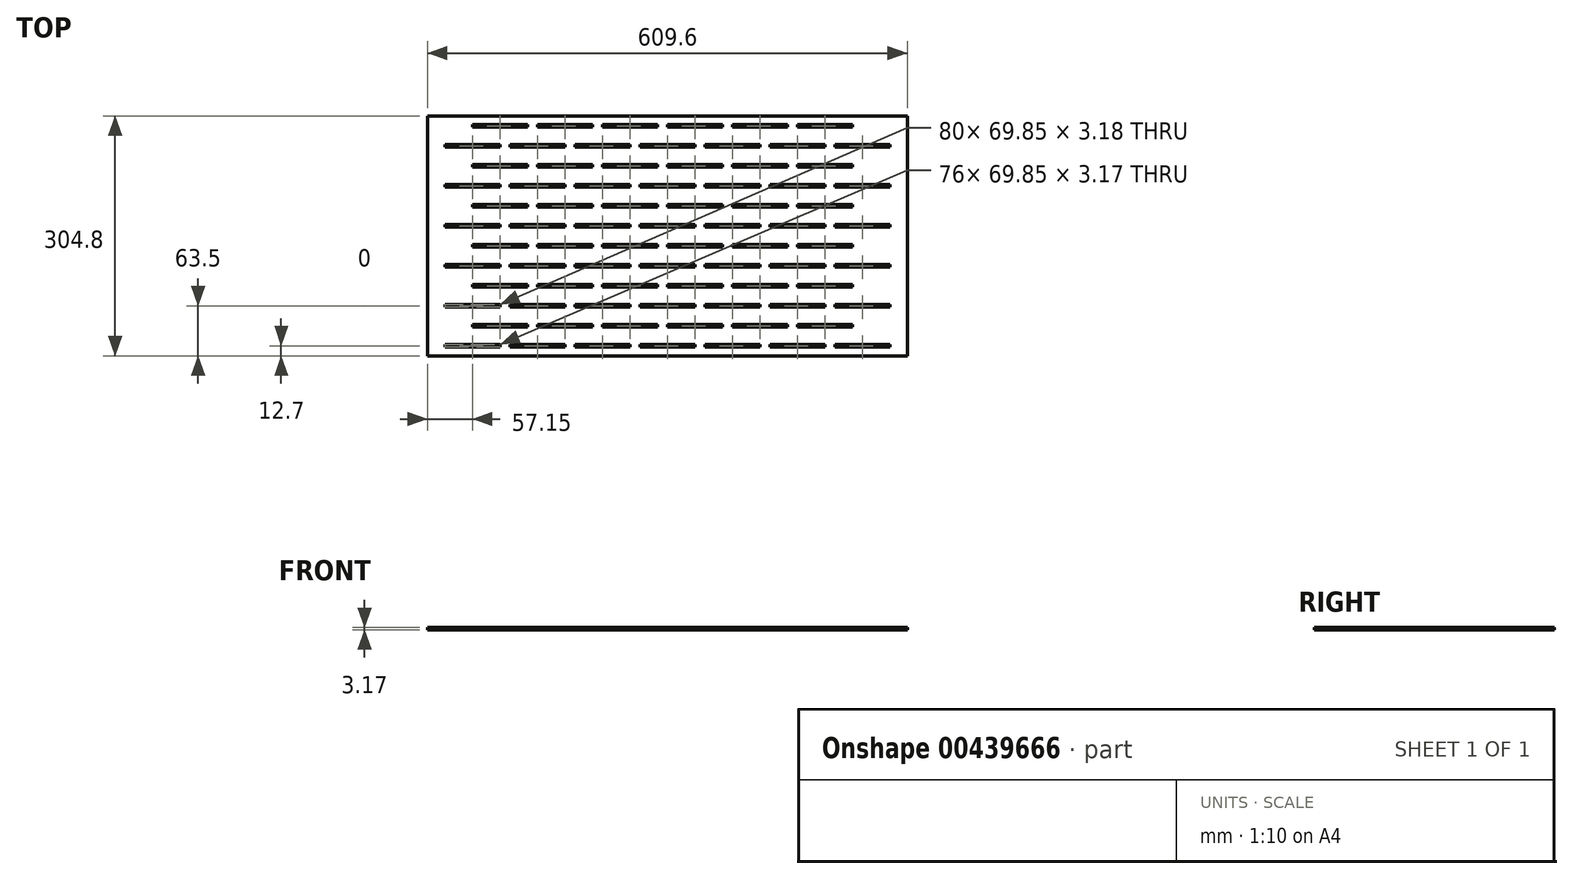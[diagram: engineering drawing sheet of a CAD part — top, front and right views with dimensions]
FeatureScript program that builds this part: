
annotation { "Feature Type Name" : "Feature", "Feature Type Description" : "" }
export const myFeature = defineFeature(function(context is Context, id is Id, definition is map)
    precondition{}
    {
        {
            var Q0;
            Q0=qCreatedBy(makeId("Top.planeOp"),FACE);
            var sketch = newSketch(context, id + "F0", { "sketchPlane" : qUnion([Q0])});
            skLineSegment(sketch, "E0.bottom", {"start": v(0, 0) * mm, "end": v(609.6, 0) * mm});
            skLineSegment(sketch, "E0.top", {"start": v(0, 304.8) * mm, "end": v(609.6, 304.8) * mm});
            skLineSegment(sketch, "E0.left", {"start": v(0, 0) * mm, "end": v(0, 304.8) * mm});
            skLineSegment(sketch, "E0.right", {"start": v(609.6, 0) * mm, "end": v(609.6, 304.8) * mm});
            skLineSegment(sketch, "E1.bottom", {"start": v(22.22, 14.29) * mm, "end": v(92.07, 14.29) * mm});
            skLineSegment(sketch, "E1.top", {"start": v(22.23, 11.11) * mm, "end": v(92.07, 11.11) * mm});
            skLineSegment(sketch, "E1.left", {"start": v(22.22, 14.29) * mm, "end": v(22.22, 11.11) * mm});
            skLineSegment(sketch, "E1.right", {"start": v(92.08, 14.29) * mm, "end": v(92.08, 11.11) * mm});
            skLineSegment(sketch, "E2.1.0.0", {"start": v(104.78, 11.11) * mm, "end": v(174.62, 11.11) * mm});
            skLineSegment(sketch, "E2.1.0.1", {"start": v(104.77, 14.29) * mm, "end": v(174.62, 14.29) * mm});
            skLineSegment(sketch, "E2.1.0.2", {"start": v(104.78, 14.29) * mm, "end": v(104.78, 11.11) * mm});
            skLineSegment(sketch, "E2.1.0.3", {"start": v(174.63, 14.29) * mm, "end": v(174.63, 11.11) * mm});
            skLineSegment(sketch, "E2.2.0.0", {"start": v(187.33, 11.11) * mm, "end": v(257.18, 11.11) * mm});
            skLineSegment(sketch, "E2.2.0.1", {"start": v(187.32, 14.29) * mm, "end": v(257.18, 14.29) * mm});
            skLineSegment(sketch, "E2.2.0.2", {"start": v(187.33, 14.29) * mm, "end": v(187.33, 11.11) * mm});
            skLineSegment(sketch, "E2.2.0.3", {"start": v(257.18, 14.29) * mm, "end": v(257.18, 11.11) * mm});
            skLineSegment(sketch, "E2.3.0.0", {"start": v(269.88, 11.11) * mm, "end": v(339.73, 11.11) * mm});
            skLineSegment(sketch, "E2.3.0.1", {"start": v(269.88, 14.29) * mm, "end": v(339.73, 14.29) * mm});
            skLineSegment(sketch, "E2.3.0.2", {"start": v(269.88, 14.29) * mm, "end": v(269.88, 11.11) * mm});
            skLineSegment(sketch, "E2.3.0.3", {"start": v(339.73, 14.29) * mm, "end": v(339.73, 11.11) * mm});
            skLineSegment(sketch, "E2.4.0.0", {"start": v(352.43, 11.11) * mm, "end": v(422.28, 11.11) * mm});
            skLineSegment(sketch, "E2.4.0.1", {"start": v(352.43, 14.29) * mm, "end": v(422.28, 14.29) * mm});
            skLineSegment(sketch, "E2.4.0.2", {"start": v(352.43, 14.29) * mm, "end": v(352.43, 11.11) * mm});
            skLineSegment(sketch, "E2.4.0.3", {"start": v(422.28, 14.29) * mm, "end": v(422.28, 11.11) * mm});
            skLineSegment(sketch, "E2.5.0.0", {"start": v(434.98, 11.11) * mm, "end": v(504.83, 11.11) * mm});
            skLineSegment(sketch, "E2.5.0.1", {"start": v(434.98, 14.29) * mm, "end": v(504.83, 14.29) * mm});
            skLineSegment(sketch, "E2.5.0.2", {"start": v(434.98, 14.29) * mm, "end": v(434.98, 11.11) * mm});
            skLineSegment(sketch, "E2.5.0.3", {"start": v(504.83, 14.29) * mm, "end": v(504.83, 11.11) * mm});
            skLineSegment(sketch, "E2.6.0.0", {"start": v(517.53, 11.11) * mm, "end": v(587.38, 11.11) * mm});
            skLineSegment(sketch, "E2.6.0.1", {"start": v(517.52, 14.29) * mm, "end": v(587.38, 14.29) * mm});
            skLineSegment(sketch, "E2.6.0.2", {"start": v(517.52, 14.29) * mm, "end": v(517.52, 11.11) * mm});
            skLineSegment(sketch, "E2.6.0.3", {"start": v(587.38, 14.29) * mm, "end": v(587.38, 11.11) * mm});
            skLineSegment(sketch, "E2.direction1", {"start": v(22.23, 11.11) * mm, "end": v(104.78, 11.11) * mm, "construction": true});
            skLineSegment(sketch, "E3.direction1", {"start": v(22.23, 11.11) * mm, "end": v(47.62, 11.11) * mm, "construction": true});
            skLineSegment(sketch, "E4.0.1.0", {"start": v(187.33, 61.91) * mm, "end": v(257.18, 61.91) * mm});
            skLineSegment(sketch, "E4.0.1.1", {"start": v(352.43, 61.91) * mm, "end": v(422.28, 61.91) * mm});
            skLineSegment(sketch, "E4.0.1.2", {"start": v(517.52, 65.09) * mm, "end": v(587.38, 65.09) * mm});
            skLineSegment(sketch, "E4.0.1.3", {"start": v(269.88, 61.91) * mm, "end": v(339.73, 61.91) * mm});
            skLineSegment(sketch, "E4.0.1.4", {"start": v(22.23, 61.91) * mm, "end": v(104.78, 61.91) * mm, "construction": true});
            skLineSegment(sketch, "E4.0.1.5", {"start": v(517.53, 61.91) * mm, "end": v(587.38, 61.91) * mm});
            skLineSegment(sketch, "E4.0.1.6", {"start": v(434.98, 61.91) * mm, "end": v(504.83, 61.91) * mm});
            skLineSegment(sketch, "E4.0.1.7", {"start": v(352.43, 65.09) * mm, "end": v(422.28, 65.09) * mm});
            skLineSegment(sketch, "E4.0.1.8", {"start": v(434.98, 65.09) * mm, "end": v(504.83, 65.09) * mm});
            skLineSegment(sketch, "E4.0.1.9", {"start": v(22.22, 65.09) * mm, "end": v(92.07, 65.09) * mm});
            skLineSegment(sketch, "E4.0.1.10", {"start": v(187.32, 65.09) * mm, "end": v(257.18, 65.09) * mm});
            skLineSegment(sketch, "E4.0.1.11", {"start": v(104.78, 61.91) * mm, "end": v(174.62, 61.91) * mm});
            skLineSegment(sketch, "E4.0.1.12", {"start": v(104.77, 65.09) * mm, "end": v(174.62, 65.09) * mm});
            skLineSegment(sketch, "E4.0.1.13", {"start": v(269.88, 65.09) * mm, "end": v(339.73, 65.09) * mm});
            skLineSegment(sketch, "E4.0.1.14", {"start": v(22.23, 61.91) * mm, "end": v(92.07, 61.91) * mm});
            skLineSegment(sketch, "E4.0.1.15", {"start": v(22.23, 61.91) * mm, "end": v(47.62, 61.91) * mm, "construction": true});
            skLineSegment(sketch, "E4.0.1.16", {"start": v(422.28, 65.09) * mm, "end": v(422.28, 61.91) * mm});
            skLineSegment(sketch, "E4.0.1.17", {"start": v(517.52, 65.09) * mm, "end": v(517.52, 61.91) * mm});
            skLineSegment(sketch, "E4.0.1.18", {"start": v(352.43, 65.09) * mm, "end": v(352.43, 61.91) * mm});
            skLineSegment(sketch, "E4.0.1.19", {"start": v(587.38, 65.09) * mm, "end": v(587.38, 61.91) * mm});
            skLineSegment(sketch, "E4.0.1.20", {"start": v(92.08, 65.09) * mm, "end": v(92.08, 61.91) * mm});
            skLineSegment(sketch, "E4.0.1.21", {"start": v(187.33, 65.09) * mm, "end": v(187.33, 61.91) * mm});
            skLineSegment(sketch, "E4.0.1.22", {"start": v(257.18, 65.09) * mm, "end": v(257.18, 61.91) * mm});
            skLineSegment(sketch, "E4.0.1.23", {"start": v(504.83, 65.09) * mm, "end": v(504.83, 61.91) * mm});
            skLineSegment(sketch, "E4.0.1.24", {"start": v(174.63, 65.09) * mm, "end": v(174.63, 61.91) * mm});
            skLineSegment(sketch, "E4.0.1.25", {"start": v(434.98, 65.09) * mm, "end": v(434.98, 61.91) * mm});
            skLineSegment(sketch, "E4.0.1.26", {"start": v(269.88, 65.09) * mm, "end": v(269.88, 61.91) * mm});
            skLineSegment(sketch, "E4.0.1.27", {"start": v(339.73, 65.09) * mm, "end": v(339.73, 61.91) * mm});
            skLineSegment(sketch, "E4.0.1.28", {"start": v(22.22, 65.09) * mm, "end": v(22.22, 61.91) * mm});
            skLineSegment(sketch, "E4.0.1.29", {"start": v(104.78, 65.09) * mm, "end": v(104.78, 61.91) * mm});
            skLineSegment(sketch, "E4.0.2.0", {"start": v(187.33, 112.71) * mm, "end": v(257.18, 112.71) * mm});
            skLineSegment(sketch, "E4.0.2.1", {"start": v(352.43, 112.71) * mm, "end": v(422.28, 112.71) * mm});
            skLineSegment(sketch, "E4.0.2.2", {"start": v(517.52, 115.89) * mm, "end": v(587.38, 115.89) * mm});
            skLineSegment(sketch, "E4.0.2.3", {"start": v(269.88, 112.71) * mm, "end": v(339.73, 112.71) * mm});
            skLineSegment(sketch, "E4.0.2.4", {"start": v(22.23, 112.71) * mm, "end": v(104.78, 112.71) * mm, "construction": true});
            skLineSegment(sketch, "E4.0.2.5", {"start": v(517.53, 112.71) * mm, "end": v(587.38, 112.71) * mm});
            skLineSegment(sketch, "E4.0.2.6", {"start": v(434.98, 112.71) * mm, "end": v(504.83, 112.71) * mm});
            skLineSegment(sketch, "E4.0.2.7", {"start": v(352.43, 115.89) * mm, "end": v(422.28, 115.89) * mm});
            skLineSegment(sketch, "E4.0.2.8", {"start": v(434.98, 115.89) * mm, "end": v(504.83, 115.89) * mm});
            skLineSegment(sketch, "E4.0.2.9", {"start": v(22.22, 115.89) * mm, "end": v(92.07, 115.89) * mm});
            skLineSegment(sketch, "E4.0.2.10", {"start": v(187.32, 115.89) * mm, "end": v(257.18, 115.89) * mm});
            skLineSegment(sketch, "E4.0.2.11", {"start": v(104.78, 112.71) * mm, "end": v(174.62, 112.71) * mm});
            skLineSegment(sketch, "E4.0.2.12", {"start": v(104.77, 115.89) * mm, "end": v(174.62, 115.89) * mm});
            skLineSegment(sketch, "E4.0.2.13", {"start": v(269.88, 115.89) * mm, "end": v(339.73, 115.89) * mm});
            skLineSegment(sketch, "E4.0.2.14", {"start": v(22.23, 112.71) * mm, "end": v(92.07, 112.71) * mm});
            skLineSegment(sketch, "E4.0.2.15", {"start": v(22.23, 112.71) * mm, "end": v(47.62, 112.71) * mm, "construction": true});
            skLineSegment(sketch, "E4.0.2.16", {"start": v(422.28, 115.89) * mm, "end": v(422.28, 112.71) * mm});
            skLineSegment(sketch, "E4.0.2.17", {"start": v(517.52, 115.89) * mm, "end": v(517.52, 112.71) * mm});
            skLineSegment(sketch, "E4.0.2.18", {"start": v(352.43, 115.89) * mm, "end": v(352.43, 112.71) * mm});
            skLineSegment(sketch, "E4.0.2.19", {"start": v(587.38, 115.89) * mm, "end": v(587.38, 112.71) * mm});
            skLineSegment(sketch, "E4.0.2.20", {"start": v(92.08, 115.89) * mm, "end": v(92.08, 112.71) * mm});
            skLineSegment(sketch, "E4.0.2.21", {"start": v(187.33, 115.89) * mm, "end": v(187.33, 112.71) * mm});
            skLineSegment(sketch, "E4.0.2.22", {"start": v(257.18, 115.89) * mm, "end": v(257.18, 112.71) * mm});
            skLineSegment(sketch, "E4.0.2.23", {"start": v(504.83, 115.89) * mm, "end": v(504.83, 112.71) * mm});
            skLineSegment(sketch, "E4.0.2.24", {"start": v(174.63, 115.89) * mm, "end": v(174.63, 112.71) * mm});
            skLineSegment(sketch, "E4.0.2.25", {"start": v(434.98, 115.89) * mm, "end": v(434.98, 112.71) * mm});
            skLineSegment(sketch, "E4.0.2.26", {"start": v(269.88, 115.89) * mm, "end": v(269.88, 112.71) * mm});
            skLineSegment(sketch, "E4.0.2.27", {"start": v(339.73, 115.89) * mm, "end": v(339.73, 112.71) * mm});
            skLineSegment(sketch, "E4.0.2.28", {"start": v(22.22, 115.89) * mm, "end": v(22.22, 112.71) * mm});
            skLineSegment(sketch, "E4.0.2.29", {"start": v(104.78, 115.89) * mm, "end": v(104.78, 112.71) * mm});
            skLineSegment(sketch, "E4.0.3.0", {"start": v(187.33, 163.51) * mm, "end": v(257.18, 163.51) * mm});
            skLineSegment(sketch, "E4.0.3.1", {"start": v(352.43, 163.51) * mm, "end": v(422.28, 163.51) * mm});
            skLineSegment(sketch, "E4.0.3.2", {"start": v(517.52, 166.69) * mm, "end": v(587.38, 166.69) * mm});
            skLineSegment(sketch, "E4.0.3.3", {"start": v(269.88, 163.51) * mm, "end": v(339.73, 163.51) * mm});
            skLineSegment(sketch, "E4.0.3.4", {"start": v(22.23, 163.51) * mm, "end": v(104.78, 163.51) * mm, "construction": true});
            skLineSegment(sketch, "E4.0.3.5", {"start": v(517.53, 163.51) * mm, "end": v(587.38, 163.51) * mm});
            skLineSegment(sketch, "E4.0.3.6", {"start": v(434.98, 163.51) * mm, "end": v(504.83, 163.51) * mm});
            skLineSegment(sketch, "E4.0.3.7", {"start": v(352.43, 166.69) * mm, "end": v(422.28, 166.69) * mm});
            skLineSegment(sketch, "E4.0.3.8", {"start": v(434.98, 166.69) * mm, "end": v(504.83, 166.69) * mm});
            skLineSegment(sketch, "E4.0.3.9", {"start": v(22.22, 166.69) * mm, "end": v(92.07, 166.69) * mm});
            skLineSegment(sketch, "E4.0.3.10", {"start": v(187.32, 166.69) * mm, "end": v(257.18, 166.69) * mm});
            skLineSegment(sketch, "E4.0.3.11", {"start": v(104.78, 163.51) * mm, "end": v(174.62, 163.51) * mm});
            skLineSegment(sketch, "E4.0.3.12", {"start": v(104.77, 166.69) * mm, "end": v(174.62, 166.69) * mm});
            skLineSegment(sketch, "E4.0.3.13", {"start": v(269.88, 166.69) * mm, "end": v(339.73, 166.69) * mm});
            skLineSegment(sketch, "E4.0.3.14", {"start": v(22.23, 163.51) * mm, "end": v(92.07, 163.51) * mm});
            skLineSegment(sketch, "E4.0.3.15", {"start": v(22.23, 163.51) * mm, "end": v(47.62, 163.51) * mm, "construction": true});
            skLineSegment(sketch, "E4.0.3.16", {"start": v(422.28, 166.69) * mm, "end": v(422.28, 163.51) * mm});
            skLineSegment(sketch, "E4.0.3.17", {"start": v(517.52, 166.69) * mm, "end": v(517.52, 163.51) * mm});
            skLineSegment(sketch, "E4.0.3.18", {"start": v(352.43, 166.69) * mm, "end": v(352.43, 163.51) * mm});
            skLineSegment(sketch, "E4.0.3.19", {"start": v(587.38, 166.69) * mm, "end": v(587.38, 163.51) * mm});
            skLineSegment(sketch, "E4.0.3.20", {"start": v(92.08, 166.69) * mm, "end": v(92.08, 163.51) * mm});
            skLineSegment(sketch, "E4.0.3.21", {"start": v(187.33, 166.69) * mm, "end": v(187.33, 163.51) * mm});
            skLineSegment(sketch, "E4.0.3.22", {"start": v(257.18, 166.69) * mm, "end": v(257.18, 163.51) * mm});
            skLineSegment(sketch, "E4.0.3.23", {"start": v(504.83, 166.69) * mm, "end": v(504.83, 163.51) * mm});
            skLineSegment(sketch, "E4.0.3.24", {"start": v(174.63, 166.69) * mm, "end": v(174.63, 163.51) * mm});
            skLineSegment(sketch, "E4.0.3.25", {"start": v(434.98, 166.69) * mm, "end": v(434.98, 163.51) * mm});
            skLineSegment(sketch, "E4.0.3.26", {"start": v(269.88, 166.69) * mm, "end": v(269.88, 163.51) * mm});
            skLineSegment(sketch, "E4.0.3.27", {"start": v(339.73, 166.69) * mm, "end": v(339.73, 163.51) * mm});
            skLineSegment(sketch, "E4.0.3.28", {"start": v(22.22, 166.69) * mm, "end": v(22.22, 163.51) * mm});
            skLineSegment(sketch, "E4.0.3.29", {"start": v(104.78, 166.69) * mm, "end": v(104.78, 163.51) * mm});
            skLineSegment(sketch, "E4.0.4.0", {"start": v(187.33, 214.31) * mm, "end": v(257.18, 214.31) * mm});
            skLineSegment(sketch, "E4.0.4.1", {"start": v(352.43, 214.31) * mm, "end": v(422.28, 214.31) * mm});
            skLineSegment(sketch, "E4.0.4.2", {"start": v(517.52, 217.49) * mm, "end": v(587.38, 217.49) * mm});
            skLineSegment(sketch, "E4.0.4.3", {"start": v(269.88, 214.31) * mm, "end": v(339.73, 214.31) * mm});
            skLineSegment(sketch, "E4.0.4.4", {"start": v(22.23, 214.31) * mm, "end": v(104.78, 214.31) * mm, "construction": true});
            skLineSegment(sketch, "E4.0.4.5", {"start": v(517.53, 214.31) * mm, "end": v(587.38, 214.31) * mm});
            skLineSegment(sketch, "E4.0.4.6", {"start": v(434.98, 214.31) * mm, "end": v(504.83, 214.31) * mm});
            skLineSegment(sketch, "E4.0.4.7", {"start": v(352.43, 217.49) * mm, "end": v(422.28, 217.49) * mm});
            skLineSegment(sketch, "E4.0.4.8", {"start": v(434.98, 217.49) * mm, "end": v(504.83, 217.49) * mm});
            skLineSegment(sketch, "E4.0.4.9", {"start": v(22.22, 217.49) * mm, "end": v(92.07, 217.49) * mm});
            skLineSegment(sketch, "E4.0.4.10", {"start": v(187.32, 217.49) * mm, "end": v(257.18, 217.49) * mm});
            skLineSegment(sketch, "E4.0.4.11", {"start": v(104.78, 214.31) * mm, "end": v(174.62, 214.31) * mm});
            skLineSegment(sketch, "E4.0.4.12", {"start": v(104.77, 217.49) * mm, "end": v(174.62, 217.49) * mm});
            skLineSegment(sketch, "E4.0.4.13", {"start": v(269.88, 217.49) * mm, "end": v(339.73, 217.49) * mm});
            skLineSegment(sketch, "E4.0.4.14", {"start": v(22.23, 214.31) * mm, "end": v(92.07, 214.31) * mm});
            skLineSegment(sketch, "E4.0.4.15", {"start": v(22.23, 214.31) * mm, "end": v(47.62, 214.31) * mm, "construction": true});
            skLineSegment(sketch, "E4.0.4.16", {"start": v(422.28, 217.49) * mm, "end": v(422.28, 214.31) * mm});
            skLineSegment(sketch, "E4.0.4.17", {"start": v(517.52, 217.49) * mm, "end": v(517.52, 214.31) * mm});
            skLineSegment(sketch, "E4.0.4.18", {"start": v(352.43, 217.49) * mm, "end": v(352.43, 214.31) * mm});
            skLineSegment(sketch, "E4.0.4.19", {"start": v(587.38, 217.49) * mm, "end": v(587.38, 214.31) * mm});
            skLineSegment(sketch, "E4.0.4.20", {"start": v(92.08, 217.49) * mm, "end": v(92.08, 214.31) * mm});
            skLineSegment(sketch, "E4.0.4.21", {"start": v(187.33, 217.49) * mm, "end": v(187.33, 214.31) * mm});
            skLineSegment(sketch, "E4.0.4.22", {"start": v(257.18, 217.49) * mm, "end": v(257.18, 214.31) * mm});
            skLineSegment(sketch, "E4.0.4.23", {"start": v(504.83, 217.49) * mm, "end": v(504.83, 214.31) * mm});
            skLineSegment(sketch, "E4.0.4.24", {"start": v(174.63, 217.49) * mm, "end": v(174.63, 214.31) * mm});
            skLineSegment(sketch, "E4.0.4.25", {"start": v(434.98, 217.49) * mm, "end": v(434.98, 214.31) * mm});
            skLineSegment(sketch, "E4.0.4.26", {"start": v(269.88, 217.49) * mm, "end": v(269.88, 214.31) * mm});
            skLineSegment(sketch, "E4.0.4.27", {"start": v(339.73, 217.49) * mm, "end": v(339.73, 214.31) * mm});
            skLineSegment(sketch, "E4.0.4.28", {"start": v(22.22, 217.49) * mm, "end": v(22.22, 214.31) * mm});
            skLineSegment(sketch, "E4.0.4.29", {"start": v(104.78, 217.49) * mm, "end": v(104.78, 214.31) * mm});
            skLineSegment(sketch, "E4.0.5.0", {"start": v(187.33, 265.11) * mm, "end": v(257.18, 265.11) * mm});
            skLineSegment(sketch, "E4.0.5.1", {"start": v(352.43, 265.11) * mm, "end": v(422.28, 265.11) * mm});
            skLineSegment(sketch, "E4.0.5.2", {"start": v(517.52, 268.29) * mm, "end": v(587.38, 268.29) * mm});
            skLineSegment(sketch, "E4.0.5.3", {"start": v(269.88, 265.11) * mm, "end": v(339.73, 265.11) * mm});
            skLineSegment(sketch, "E4.0.5.4", {"start": v(22.23, 265.11) * mm, "end": v(104.78, 265.11) * mm, "construction": true});
            skLineSegment(sketch, "E4.0.5.5", {"start": v(517.53, 265.11) * mm, "end": v(587.38, 265.11) * mm});
            skLineSegment(sketch, "E4.0.5.6", {"start": v(434.98, 265.11) * mm, "end": v(504.83, 265.11) * mm});
            skLineSegment(sketch, "E4.0.5.7", {"start": v(352.43, 268.29) * mm, "end": v(422.28, 268.29) * mm});
            skLineSegment(sketch, "E4.0.5.8", {"start": v(434.98, 268.29) * mm, "end": v(504.83, 268.29) * mm});
            skLineSegment(sketch, "E4.0.5.9", {"start": v(22.22, 268.29) * mm, "end": v(92.07, 268.29) * mm});
            skLineSegment(sketch, "E4.0.5.10", {"start": v(187.32, 268.29) * mm, "end": v(257.18, 268.29) * mm});
            skLineSegment(sketch, "E4.0.5.11", {"start": v(104.78, 265.11) * mm, "end": v(174.62, 265.11) * mm});
            skLineSegment(sketch, "E4.0.5.12", {"start": v(104.77, 268.29) * mm, "end": v(174.62, 268.29) * mm});
            skLineSegment(sketch, "E4.0.5.13", {"start": v(269.88, 268.29) * mm, "end": v(339.73, 268.29) * mm});
            skLineSegment(sketch, "E4.0.5.14", {"start": v(22.23, 265.11) * mm, "end": v(92.07, 265.11) * mm});
            skLineSegment(sketch, "E4.0.5.15", {"start": v(22.23, 265.11) * mm, "end": v(47.62, 265.11) * mm, "construction": true});
            skLineSegment(sketch, "E4.0.5.16", {"start": v(422.28, 268.29) * mm, "end": v(422.28, 265.11) * mm});
            skLineSegment(sketch, "E4.0.5.17", {"start": v(517.52, 268.29) * mm, "end": v(517.52, 265.11) * mm});
            skLineSegment(sketch, "E4.0.5.18", {"start": v(352.43, 268.29) * mm, "end": v(352.43, 265.11) * mm});
            skLineSegment(sketch, "E4.0.5.19", {"start": v(587.38, 268.29) * mm, "end": v(587.38, 265.11) * mm});
            skLineSegment(sketch, "E4.0.5.20", {"start": v(92.08, 268.29) * mm, "end": v(92.08, 265.11) * mm});
            skLineSegment(sketch, "E4.0.5.21", {"start": v(187.33, 268.29) * mm, "end": v(187.33, 265.11) * mm});
            skLineSegment(sketch, "E4.0.5.22", {"start": v(257.18, 268.29) * mm, "end": v(257.18, 265.11) * mm});
            skLineSegment(sketch, "E4.0.5.23", {"start": v(504.83, 268.29) * mm, "end": v(504.83, 265.11) * mm});
            skLineSegment(sketch, "E4.0.5.24", {"start": v(174.63, 268.29) * mm, "end": v(174.63, 265.11) * mm});
            skLineSegment(sketch, "E4.0.5.25", {"start": v(434.98, 268.29) * mm, "end": v(434.98, 265.11) * mm});
            skLineSegment(sketch, "E4.0.5.26", {"start": v(269.88, 268.29) * mm, "end": v(269.88, 265.11) * mm});
            skLineSegment(sketch, "E4.0.5.27", {"start": v(339.73, 268.29) * mm, "end": v(339.73, 265.11) * mm});
            skLineSegment(sketch, "E4.0.5.28", {"start": v(22.22, 268.29) * mm, "end": v(22.22, 265.11) * mm});
            skLineSegment(sketch, "E4.0.5.29", {"start": v(104.78, 268.29) * mm, "end": v(104.78, 265.11) * mm});
            skLineSegment(sketch, "E4.direction1", {"start": v(22.22, 11.11) * mm, "end": v(47.62, 11.11) * mm, "construction": true});
            skLineSegment(sketch, "E4.direction2", {"start": v(22.22, 11.11) * mm, "end": v(22.22, 61.91) * mm, "construction": true});
            skLineSegment(sketch, "E5.bottom", {"start": v(57.15, 39.69) * mm, "end": v(127, 39.69) * mm});
            skLineSegment(sketch, "E5.top", {"start": v(57.15, 36.51) * mm, "end": v(127, 36.51) * mm});
            skLineSegment(sketch, "E5.left", {"start": v(57.15, 39.69) * mm, "end": v(57.15, 36.51) * mm});
            skLineSegment(sketch, "E5.right", {"start": v(127, 39.69) * mm, "end": v(127, 36.51) * mm});
            skLineSegment(sketch, "E6.1.0.0", {"start": v(139.7, 36.51) * mm, "end": v(209.55, 36.51) * mm});
            skLineSegment(sketch, "E6.1.0.1", {"start": v(139.7, 39.69) * mm, "end": v(209.55, 39.69) * mm});
            skLineSegment(sketch, "E6.1.0.2", {"start": v(139.7, 39.69) * mm, "end": v(139.7, 36.51) * mm});
            skLineSegment(sketch, "E6.1.0.3", {"start": v(209.55, 39.69) * mm, "end": v(209.55, 36.51) * mm});
            skLineSegment(sketch, "E6.2.0.0", {"start": v(222.25, 36.51) * mm, "end": v(292.1, 36.51) * mm});
            skLineSegment(sketch, "E6.2.0.1", {"start": v(222.25, 39.69) * mm, "end": v(292.1, 39.69) * mm});
            skLineSegment(sketch, "E6.2.0.2", {"start": v(222.25, 39.69) * mm, "end": v(222.25, 36.51) * mm});
            skLineSegment(sketch, "E6.2.0.3", {"start": v(292.1, 39.69) * mm, "end": v(292.1, 36.51) * mm});
            skLineSegment(sketch, "E6.3.0.0", {"start": v(304.8, 36.51) * mm, "end": v(374.65, 36.51) * mm});
            skLineSegment(sketch, "E6.3.0.1", {"start": v(304.8, 39.69) * mm, "end": v(374.65, 39.69) * mm});
            skLineSegment(sketch, "E6.3.0.2", {"start": v(304.8, 39.69) * mm, "end": v(304.8, 36.51) * mm});
            skLineSegment(sketch, "E6.3.0.3", {"start": v(374.65, 39.69) * mm, "end": v(374.65, 36.51) * mm});
            skLineSegment(sketch, "E6.4.0.0", {"start": v(387.35, 36.51) * mm, "end": v(457.2, 36.51) * mm});
            skLineSegment(sketch, "E6.4.0.1", {"start": v(387.35, 39.69) * mm, "end": v(457.2, 39.69) * mm});
            skLineSegment(sketch, "E6.4.0.2", {"start": v(387.35, 39.69) * mm, "end": v(387.35, 36.51) * mm});
            skLineSegment(sketch, "E6.4.0.3", {"start": v(457.2, 39.69) * mm, "end": v(457.2, 36.51) * mm});
            skLineSegment(sketch, "E6.5.0.0", {"start": v(469.9, 36.51) * mm, "end": v(539.75, 36.51) * mm});
            skLineSegment(sketch, "E6.5.0.1", {"start": v(469.9, 39.69) * mm, "end": v(539.75, 39.69) * mm});
            skLineSegment(sketch, "E6.5.0.2", {"start": v(469.9, 39.69) * mm, "end": v(469.9, 36.51) * mm});
            skLineSegment(sketch, "E6.5.0.3", {"start": v(539.75, 39.69) * mm, "end": v(539.75, 36.51) * mm});
            skLineSegment(sketch, "E6.direction1", {"start": v(57.15, 36.51) * mm, "end": v(139.7, 36.51) * mm, "construction": true});
            skLineSegment(sketch, "E7.direction1", {"start": v(57.15, 36.51) * mm, "end": v(82.55, 36.51) * mm, "construction": true});
            skLineSegment(sketch, "E8.0.1.0", {"start": v(222.25, 87.31) * mm, "end": v(292.1, 87.31) * mm});
            skLineSegment(sketch, "E8.0.1.1", {"start": v(387.35, 87.31) * mm, "end": v(457.2, 87.31) * mm});
            skLineSegment(sketch, "E8.0.1.3", {"start": v(304.8, 87.31) * mm, "end": v(374.65, 87.31) * mm});
            skLineSegment(sketch, "E8.0.1.4", {"start": v(57.15, 87.31) * mm, "end": v(139.7, 87.31) * mm, "construction": true});
            skLineSegment(sketch, "E8.0.1.6", {"start": v(469.9, 87.31) * mm, "end": v(539.75, 87.31) * mm});
            skLineSegment(sketch, "E8.0.1.7", {"start": v(387.35, 90.49) * mm, "end": v(457.2, 90.49) * mm});
            skLineSegment(sketch, "E8.0.1.8", {"start": v(469.9, 90.49) * mm, "end": v(539.75, 90.49) * mm});
            skLineSegment(sketch, "E8.0.1.9", {"start": v(57.15, 90.49) * mm, "end": v(127, 90.49) * mm});
            skLineSegment(sketch, "E8.0.1.10", {"start": v(222.25, 90.49) * mm, "end": v(292.1, 90.49) * mm});
            skLineSegment(sketch, "E8.0.1.11", {"start": v(139.7, 87.31) * mm, "end": v(209.55, 87.31) * mm});
            skLineSegment(sketch, "E8.0.1.12", {"start": v(139.7, 90.49) * mm, "end": v(209.55, 90.49) * mm});
            skLineSegment(sketch, "E8.0.1.13", {"start": v(304.8, 90.49) * mm, "end": v(374.65, 90.49) * mm});
            skLineSegment(sketch, "E8.0.1.14", {"start": v(57.15, 87.31) * mm, "end": v(127, 87.31) * mm});
            skLineSegment(sketch, "E8.0.1.15", {"start": v(57.15, 87.31) * mm, "end": v(82.55, 87.31) * mm, "construction": true});
            skLineSegment(sketch, "E8.0.1.16", {"start": v(457.2, 90.49) * mm, "end": v(457.2, 87.31) * mm});
            skLineSegment(sketch, "E8.0.1.18", {"start": v(387.35, 90.49) * mm, "end": v(387.35, 87.31) * mm});
            skLineSegment(sketch, "E8.0.1.20", {"start": v(127, 90.49) * mm, "end": v(127, 87.31) * mm});
            skLineSegment(sketch, "E8.0.1.21", {"start": v(222.25, 90.49) * mm, "end": v(222.25, 87.31) * mm});
            skLineSegment(sketch, "E8.0.1.22", {"start": v(292.1, 90.49) * mm, "end": v(292.1, 87.31) * mm});
            skLineSegment(sketch, "E8.0.1.23", {"start": v(539.75, 90.49) * mm, "end": v(539.75, 87.31) * mm});
            skLineSegment(sketch, "E8.0.1.24", {"start": v(209.55, 90.49) * mm, "end": v(209.55, 87.31) * mm});
            skLineSegment(sketch, "E8.0.1.25", {"start": v(469.9, 90.49) * mm, "end": v(469.9, 87.31) * mm});
            skLineSegment(sketch, "E8.0.1.26", {"start": v(304.8, 90.49) * mm, "end": v(304.8, 87.31) * mm});
            skLineSegment(sketch, "E8.0.1.27", {"start": v(374.65, 90.49) * mm, "end": v(374.65, 87.31) * mm});
            skLineSegment(sketch, "E8.0.1.28", {"start": v(57.15, 90.49) * mm, "end": v(57.15, 87.31) * mm});
            skLineSegment(sketch, "E8.0.1.29", {"start": v(139.7, 90.49) * mm, "end": v(139.7, 87.31) * mm});
            skLineSegment(sketch, "E8.0.2.0", {"start": v(222.25, 138.11) * mm, "end": v(292.1, 138.11) * mm});
            skLineSegment(sketch, "E8.0.2.1", {"start": v(387.35, 138.11) * mm, "end": v(457.2, 138.11) * mm});
            skLineSegment(sketch, "E8.0.2.3", {"start": v(304.8, 138.11) * mm, "end": v(374.65, 138.11) * mm});
            skLineSegment(sketch, "E8.0.2.4", {"start": v(57.15, 138.11) * mm, "end": v(139.7, 138.11) * mm, "construction": true});
            skLineSegment(sketch, "E8.0.2.6", {"start": v(469.9, 138.11) * mm, "end": v(539.75, 138.11) * mm});
            skLineSegment(sketch, "E8.0.2.7", {"start": v(387.35, 141.29) * mm, "end": v(457.2, 141.29) * mm});
            skLineSegment(sketch, "E8.0.2.8", {"start": v(469.9, 141.29) * mm, "end": v(539.75, 141.29) * mm});
            skLineSegment(sketch, "E8.0.2.9", {"start": v(57.15, 141.29) * mm, "end": v(127, 141.29) * mm});
            skLineSegment(sketch, "E8.0.2.10", {"start": v(222.25, 141.29) * mm, "end": v(292.1, 141.29) * mm});
            skLineSegment(sketch, "E8.0.2.11", {"start": v(139.7, 138.11) * mm, "end": v(209.55, 138.11) * mm});
            skLineSegment(sketch, "E8.0.2.12", {"start": v(139.7, 141.29) * mm, "end": v(209.55, 141.29) * mm});
            skLineSegment(sketch, "E8.0.2.13", {"start": v(304.8, 141.29) * mm, "end": v(374.65, 141.29) * mm});
            skLineSegment(sketch, "E8.0.2.14", {"start": v(57.15, 138.11) * mm, "end": v(127, 138.11) * mm});
            skLineSegment(sketch, "E8.0.2.15", {"start": v(57.15, 138.11) * mm, "end": v(82.55, 138.11) * mm, "construction": true});
            skLineSegment(sketch, "E8.0.2.16", {"start": v(457.2, 141.29) * mm, "end": v(457.2, 138.11) * mm});
            skLineSegment(sketch, "E8.0.2.18", {"start": v(387.35, 141.29) * mm, "end": v(387.35, 138.11) * mm});
            skLineSegment(sketch, "E8.0.2.20", {"start": v(127, 141.29) * mm, "end": v(127, 138.11) * mm});
            skLineSegment(sketch, "E8.0.2.21", {"start": v(222.25, 141.29) * mm, "end": v(222.25, 138.11) * mm});
            skLineSegment(sketch, "E8.0.2.22", {"start": v(292.1, 141.29) * mm, "end": v(292.1, 138.11) * mm});
            skLineSegment(sketch, "E8.0.2.23", {"start": v(539.75, 141.29) * mm, "end": v(539.75, 138.11) * mm});
            skLineSegment(sketch, "E8.0.2.24", {"start": v(209.55, 141.29) * mm, "end": v(209.55, 138.11) * mm});
            skLineSegment(sketch, "E8.0.2.25", {"start": v(469.9, 141.29) * mm, "end": v(469.9, 138.11) * mm});
            skLineSegment(sketch, "E8.0.2.26", {"start": v(304.8, 141.29) * mm, "end": v(304.8, 138.11) * mm});
            skLineSegment(sketch, "E8.0.2.27", {"start": v(374.65, 141.29) * mm, "end": v(374.65, 138.11) * mm});
            skLineSegment(sketch, "E8.0.2.28", {"start": v(57.15, 141.29) * mm, "end": v(57.15, 138.11) * mm});
            skLineSegment(sketch, "E8.0.2.29", {"start": v(139.7, 141.29) * mm, "end": v(139.7, 138.11) * mm});
            skLineSegment(sketch, "E8.0.3.0", {"start": v(222.25, 188.91) * mm, "end": v(292.1, 188.91) * mm});
            skLineSegment(sketch, "E8.0.3.1", {"start": v(387.35, 188.91) * mm, "end": v(457.2, 188.91) * mm});
            skLineSegment(sketch, "E8.0.3.3", {"start": v(304.8, 188.91) * mm, "end": v(374.65, 188.91) * mm});
            skLineSegment(sketch, "E8.0.3.4", {"start": v(57.15, 188.91) * mm, "end": v(139.7, 188.91) * mm, "construction": true});
            skLineSegment(sketch, "E8.0.3.6", {"start": v(469.9, 188.91) * mm, "end": v(539.75, 188.91) * mm});
            skLineSegment(sketch, "E8.0.3.7", {"start": v(387.35, 192.09) * mm, "end": v(457.2, 192.09) * mm});
            skLineSegment(sketch, "E8.0.3.8", {"start": v(469.9, 192.09) * mm, "end": v(539.75, 192.09) * mm});
            skLineSegment(sketch, "E8.0.3.9", {"start": v(57.15, 192.09) * mm, "end": v(127, 192.09) * mm});
            skLineSegment(sketch, "E8.0.3.10", {"start": v(222.25, 192.09) * mm, "end": v(292.1, 192.09) * mm});
            skLineSegment(sketch, "E8.0.3.11", {"start": v(139.7, 188.91) * mm, "end": v(209.55, 188.91) * mm});
            skLineSegment(sketch, "E8.0.3.12", {"start": v(139.7, 192.09) * mm, "end": v(209.55, 192.09) * mm});
            skLineSegment(sketch, "E8.0.3.13", {"start": v(304.8, 192.09) * mm, "end": v(374.65, 192.09) * mm});
            skLineSegment(sketch, "E8.0.3.14", {"start": v(57.15, 188.91) * mm, "end": v(127, 188.91) * mm});
            skLineSegment(sketch, "E8.0.3.15", {"start": v(57.15, 188.91) * mm, "end": v(82.55, 188.91) * mm, "construction": true});
            skLineSegment(sketch, "E8.0.3.16", {"start": v(457.2, 192.09) * mm, "end": v(457.2, 188.91) * mm});
            skLineSegment(sketch, "E8.0.3.18", {"start": v(387.35, 192.09) * mm, "end": v(387.35, 188.91) * mm});
            skLineSegment(sketch, "E8.0.3.20", {"start": v(127, 192.09) * mm, "end": v(127, 188.91) * mm});
            skLineSegment(sketch, "E8.0.3.21", {"start": v(222.25, 192.09) * mm, "end": v(222.25, 188.91) * mm});
            skLineSegment(sketch, "E8.0.3.22", {"start": v(292.1, 192.09) * mm, "end": v(292.1, 188.91) * mm});
            skLineSegment(sketch, "E8.0.3.23", {"start": v(539.75, 192.09) * mm, "end": v(539.75, 188.91) * mm});
            skLineSegment(sketch, "E8.0.3.24", {"start": v(209.55, 192.09) * mm, "end": v(209.55, 188.91) * mm});
            skLineSegment(sketch, "E8.0.3.25", {"start": v(469.9, 192.09) * mm, "end": v(469.9, 188.91) * mm});
            skLineSegment(sketch, "E8.0.3.26", {"start": v(304.8, 192.09) * mm, "end": v(304.8, 188.91) * mm});
            skLineSegment(sketch, "E8.0.3.27", {"start": v(374.65, 192.09) * mm, "end": v(374.65, 188.91) * mm});
            skLineSegment(sketch, "E8.0.3.28", {"start": v(57.15, 192.09) * mm, "end": v(57.15, 188.91) * mm});
            skLineSegment(sketch, "E8.0.3.29", {"start": v(139.7, 192.09) * mm, "end": v(139.7, 188.91) * mm});
            skLineSegment(sketch, "E8.0.4.0", {"start": v(222.25, 239.71) * mm, "end": v(292.1, 239.71) * mm});
            skLineSegment(sketch, "E8.0.4.1", {"start": v(387.35, 239.71) * mm, "end": v(457.2, 239.71) * mm});
            skLineSegment(sketch, "E8.0.4.3", {"start": v(304.8, 239.71) * mm, "end": v(374.65, 239.71) * mm});
            skLineSegment(sketch, "E8.0.4.4", {"start": v(57.15, 239.71) * mm, "end": v(139.7, 239.71) * mm, "construction": true});
            skLineSegment(sketch, "E8.0.4.6", {"start": v(469.9, 239.71) * mm, "end": v(539.75, 239.71) * mm});
            skLineSegment(sketch, "E8.0.4.7", {"start": v(387.35, 242.89) * mm, "end": v(457.2, 242.89) * mm});
            skLineSegment(sketch, "E8.0.4.8", {"start": v(469.9, 242.89) * mm, "end": v(539.75, 242.89) * mm});
            skLineSegment(sketch, "E8.0.4.9", {"start": v(57.15, 242.89) * mm, "end": v(127, 242.89) * mm});
            skLineSegment(sketch, "E8.0.4.10", {"start": v(222.25, 242.89) * mm, "end": v(292.1, 242.89) * mm});
            skLineSegment(sketch, "E8.0.4.11", {"start": v(139.7, 239.71) * mm, "end": v(209.55, 239.71) * mm});
            skLineSegment(sketch, "E8.0.4.12", {"start": v(139.7, 242.89) * mm, "end": v(209.55, 242.89) * mm});
            skLineSegment(sketch, "E8.0.4.13", {"start": v(304.8, 242.89) * mm, "end": v(374.65, 242.89) * mm});
            skLineSegment(sketch, "E8.0.4.14", {"start": v(57.15, 239.71) * mm, "end": v(127, 239.71) * mm});
            skLineSegment(sketch, "E8.0.4.15", {"start": v(57.15, 239.71) * mm, "end": v(82.55, 239.71) * mm, "construction": true});
            skLineSegment(sketch, "E8.0.4.16", {"start": v(457.2, 242.89) * mm, "end": v(457.2, 239.71) * mm});
            skLineSegment(sketch, "E8.0.4.18", {"start": v(387.35, 242.89) * mm, "end": v(387.35, 239.71) * mm});
            skLineSegment(sketch, "E8.0.4.20", {"start": v(127, 242.89) * mm, "end": v(127, 239.71) * mm});
            skLineSegment(sketch, "E8.0.4.21", {"start": v(222.25, 242.89) * mm, "end": v(222.25, 239.71) * mm});
            skLineSegment(sketch, "E8.0.4.22", {"start": v(292.1, 242.89) * mm, "end": v(292.1, 239.71) * mm});
            skLineSegment(sketch, "E8.0.4.23", {"start": v(539.75, 242.89) * mm, "end": v(539.75, 239.71) * mm});
            skLineSegment(sketch, "E8.0.4.24", {"start": v(209.55, 242.89) * mm, "end": v(209.55, 239.71) * mm});
            skLineSegment(sketch, "E8.0.4.25", {"start": v(469.9, 242.89) * mm, "end": v(469.9, 239.71) * mm});
            skLineSegment(sketch, "E8.0.4.26", {"start": v(304.8, 242.89) * mm, "end": v(304.8, 239.71) * mm});
            skLineSegment(sketch, "E8.0.4.27", {"start": v(374.65, 242.89) * mm, "end": v(374.65, 239.71) * mm});
            skLineSegment(sketch, "E8.0.4.28", {"start": v(57.15, 242.89) * mm, "end": v(57.15, 239.71) * mm});
            skLineSegment(sketch, "E8.0.4.29", {"start": v(139.7, 242.89) * mm, "end": v(139.7, 239.71) * mm});
            skLineSegment(sketch, "E8.0.5.0", {"start": v(222.25, 290.51) * mm, "end": v(292.1, 290.51) * mm});
            skLineSegment(sketch, "E8.0.5.1", {"start": v(387.35, 290.51) * mm, "end": v(457.2, 290.51) * mm});
            skLineSegment(sketch, "E8.0.5.3", {"start": v(304.8, 290.51) * mm, "end": v(374.65, 290.51) * mm});
            skLineSegment(sketch, "E8.0.5.4", {"start": v(57.15, 290.51) * mm, "end": v(139.7, 290.51) * mm, "construction": true});
            skLineSegment(sketch, "E8.0.5.6", {"start": v(469.9, 290.51) * mm, "end": v(539.75, 290.51) * mm});
            skLineSegment(sketch, "E8.0.5.7", {"start": v(387.35, 293.69) * mm, "end": v(457.2, 293.69) * mm});
            skLineSegment(sketch, "E8.0.5.8", {"start": v(469.9, 293.69) * mm, "end": v(539.75, 293.69) * mm});
            skLineSegment(sketch, "E8.0.5.9", {"start": v(57.15, 293.69) * mm, "end": v(127, 293.69) * mm});
            skLineSegment(sketch, "E8.0.5.10", {"start": v(222.25, 293.69) * mm, "end": v(292.1, 293.69) * mm});
            skLineSegment(sketch, "E8.0.5.11", {"start": v(139.7, 290.51) * mm, "end": v(209.55, 290.51) * mm});
            skLineSegment(sketch, "E8.0.5.12", {"start": v(139.7, 293.69) * mm, "end": v(209.55, 293.69) * mm});
            skLineSegment(sketch, "E8.0.5.13", {"start": v(304.8, 293.69) * mm, "end": v(374.65, 293.69) * mm});
            skLineSegment(sketch, "E8.0.5.14", {"start": v(57.15, 290.51) * mm, "end": v(127, 290.51) * mm});
            skLineSegment(sketch, "E8.0.5.15", {"start": v(57.15, 290.51) * mm, "end": v(82.55, 290.51) * mm, "construction": true});
            skLineSegment(sketch, "E8.0.5.16", {"start": v(457.2, 293.69) * mm, "end": v(457.2, 290.51) * mm});
            skLineSegment(sketch, "E8.0.5.18", {"start": v(387.35, 293.69) * mm, "end": v(387.35, 290.51) * mm});
            skLineSegment(sketch, "E8.0.5.20", {"start": v(127, 293.69) * mm, "end": v(127, 290.51) * mm});
            skLineSegment(sketch, "E8.0.5.21", {"start": v(222.25, 293.69) * mm, "end": v(222.25, 290.51) * mm});
            skLineSegment(sketch, "E8.0.5.22", {"start": v(292.1, 293.69) * mm, "end": v(292.1, 290.51) * mm});
            skLineSegment(sketch, "E8.0.5.23", {"start": v(539.75, 293.69) * mm, "end": v(539.75, 290.51) * mm});
            skLineSegment(sketch, "E8.0.5.24", {"start": v(209.55, 293.69) * mm, "end": v(209.55, 290.51) * mm});
            skLineSegment(sketch, "E8.0.5.25", {"start": v(469.9, 293.69) * mm, "end": v(469.9, 290.51) * mm});
            skLineSegment(sketch, "E8.0.5.26", {"start": v(304.8, 293.69) * mm, "end": v(304.8, 290.51) * mm});
            skLineSegment(sketch, "E8.0.5.27", {"start": v(374.65, 293.69) * mm, "end": v(374.65, 290.51) * mm});
            skLineSegment(sketch, "E8.0.5.28", {"start": v(57.15, 293.69) * mm, "end": v(57.15, 290.51) * mm});
            skLineSegment(sketch, "E8.0.5.29", {"start": v(139.7, 293.69) * mm, "end": v(139.7, 290.51) * mm});
            skLineSegment(sketch, "E8.direction2", {"start": v(57.15, 36.51) * mm, "end": v(57.15, 87.31) * mm, "construction": true});
            skPoint(sketch, "E9", {"position": v(57.15, 14.29) * mm});
            skSolve(sketch);
        }
        {
            var Q0;
            Q0 = qSketchRegion(id + "F0", true);
            extrude(context, id + "F1", {"entities" : qUnion([Q0]), "depth" : 3.17 * mm});
        }
    });
